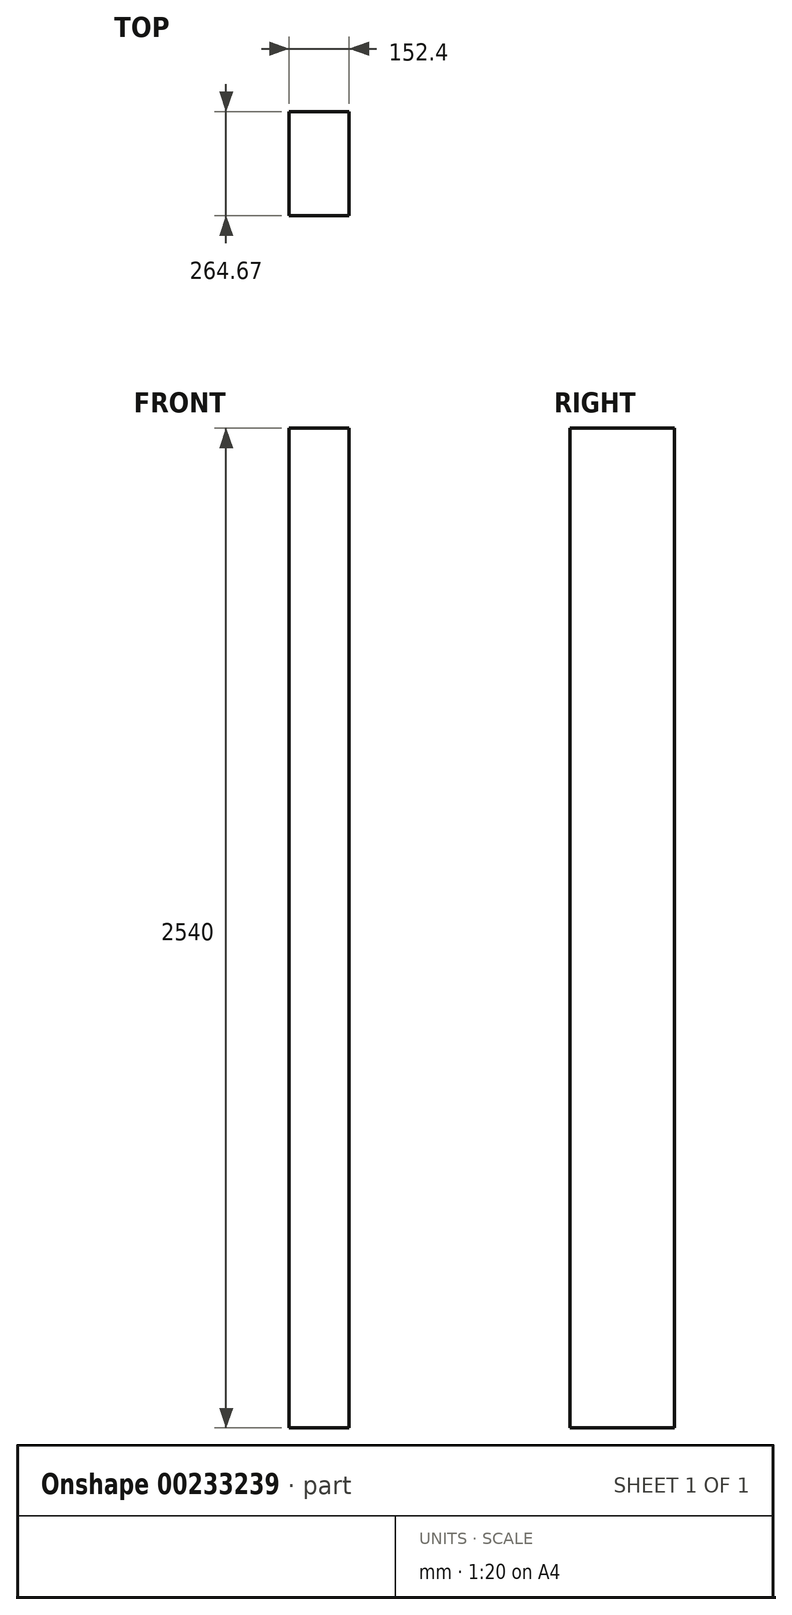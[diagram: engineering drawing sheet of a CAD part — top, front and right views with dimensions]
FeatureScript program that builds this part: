
annotation { "Feature Type Name" : "Feature", "Feature Type Description" : "" }
export const myFeature = defineFeature(function(context is Context, id is Id, definition is map)
    precondition{}
    {
        {
            var Q0;
            Q0=qCreatedBy(makeId("Right.planeOp"),FACE);
            var sketch = newSketch(context, id + "F0", { "sketchPlane" : qUnion([Q0])});
            skLineSegment(sketch, "E0.bottom", {"start": v(82.27, 1151.98) * mm, "end": v(-182.4, 1151.98) * mm});
            skLineSegment(sketch, "E0.top", {"start": v(82.27, -1388.02) * mm, "end": v(-182.4, -1388.02) * mm});
            skLineSegment(sketch, "E0.left", {"start": v(82.27, 1151.98) * mm, "end": v(82.27, -1388.02) * mm});
            skLineSegment(sketch, "E0.right", {"start": v(-182.4, 1151.98) * mm, "end": v(-182.4, -1388.02) * mm});
            skSolve(sketch);
        }
        {
            var Q0;
            Q0=makeQuery(id+"F0.imprint","IMPRINT",FACE,{"disambiguationData":[TD([[makeQuery(id+"F0.imprint","IMPRINT",EDGE,{"derivedFrom":sQuery(id+"F0.wireOp",EDGE,"E0.bottom")}),1.0]])]});
            extrude(context, id + "F1", {"entities" : qUnion([Q0]), "depth" : 152.4 * mm});
        }
    });
